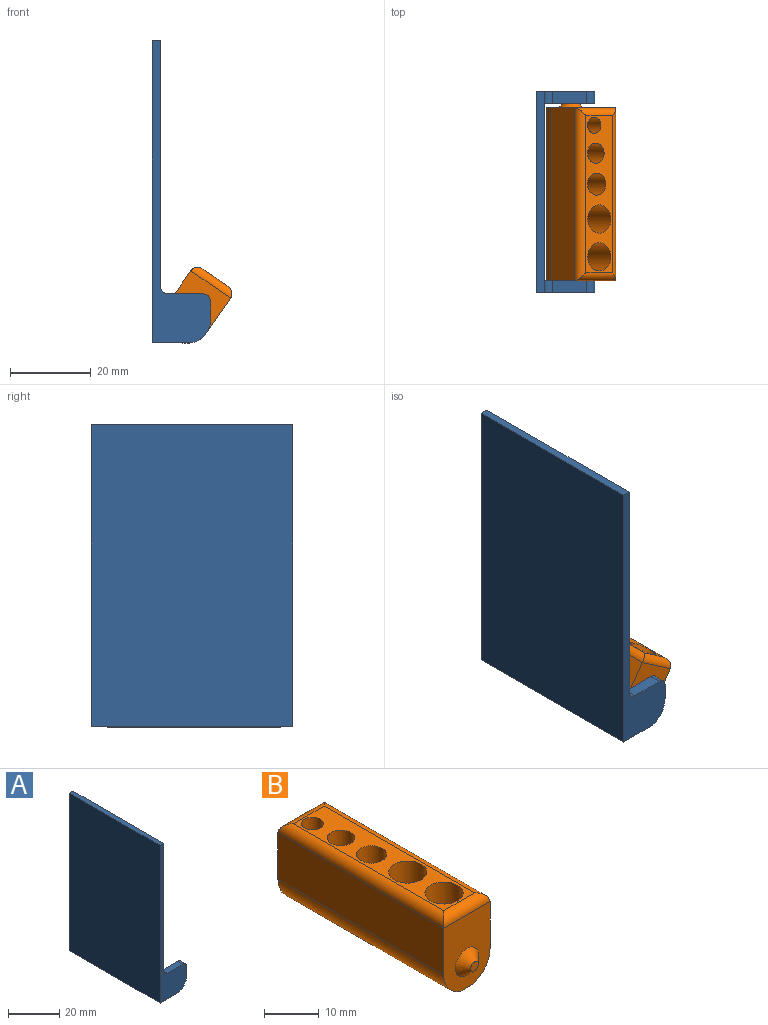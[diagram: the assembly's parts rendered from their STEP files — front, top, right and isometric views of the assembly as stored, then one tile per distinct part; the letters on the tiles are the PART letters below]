
ASSEMBLY  parts=2 mates=1
PART A: 22 faces, bbox 14.6x50x75 mm
  f0: plane 50x2mm, normal (0,0,1), area 100mm2, adj f1,f3,f4,f5
  f1: plane 75x50mm, normal (-1,0,0), area 3750mm2, adj f0,f2,f4,f5
  f2: plane 50x10.14mm, normal (0,0,-1), area 148.8mm2, adj f1,f3,f4,f5,f8,f9,f14,f15
  f3: plane 75x50mm, normal (1,0,0), area 3665.4mm2, adj f0,f2,f4,f5,f9,f15,f18,f21
  f4: plane 75x14.6mm, normal (0,-1,0), area 295.7mm2, adj f0,f1,f2,f3,f6,f7,f8,f20
  f5: plane 75x14.6mm, normal (0,1,0), area 295.7mm2, adj f0,f1,f2,f3,f12,f13,f14,f18
  f6: plane 4.3x3mm, normal (1,0,0), area 12.9mm2, adj f4,f8,f9,f20
  f7: plane 8.6x3mm, normal (0,0,1), area 25.8mm2, adj f4,f9,f20,f21
  f8: cylinder r=6mm len=5.8mm, axis (0,-1,0), area 23.6mm2, adj f2,f4,f6,f9
  f9: plane 14.1x12.6mm, normal (0,1,0), area 117.5mm2, adj f2,f3,f6,f7,f8,f10,f20,f21
  f10: cone r=3mm half-angle=45deg, axis (0,1,0), area 35.5mm2, adj f9,f11
  f11: plane 2x2mm, normal (0,1,0), area 3.1mm2, adj f10
  f12: plane 4.3x3mm, normal (1,0,0), area 12.9mm2, adj f5,f14,f15,f19
  f13: plane 8.6x3mm, normal (0,0,1), area 25.8mm2, adj f5,f15,f18,f19
  f14: cylinder r=6mm len=5.8mm, axis (0,1,0), area 23.6mm2, adj f2,f5,f12,f15
  f15: plane 14.1x12.6mm, normal (0,-1,0), area 117.5mm2, adj f2,f3,f12,f13,f14,f16,f18,f19
  f16: cone r=3mm half-angle=45deg, axis (0,-1,0), area 35.5mm2, adj f15,f17
  f17: plane 2x2mm, normal (0,-1,0), area 3.1mm2, adj f16
  f18: cylinder r=2mm len=3mm, axis (0,-1,0), area 9.4mm2, adj f3,f5,f13,f15
  f19: cylinder r=2mm len=3mm, axis (0,-1,0), area 9.4mm2, adj f5,f12,f13,f15
  f20: cylinder r=2mm len=3mm, axis (0,1,0), area 9.4mm2, adj f4,f6,f7,f9
  f21: cylinder r=2mm len=3mm, axis (0,1,0), area 9.4mm2, adj f3,f4,f7,f9
PART B: 26 faces, bbox 12x47x18.3 mm
  f0: plane 43x10.5mm, normal (-1,0,0), area 451.5mm2, adj f1,f6,f9,f23
  f1: cylinder r=6mm len=43mm, axis (0,1,0), area 338.5mm2, adj f0,f2,f6,f9
  f2: plane 43x3.07mm, normal (0,0,-1), area 132.1mm2, adj f1,f3,f6,f9
  f3: cylinder r=6mm len=43mm, axis (0,1,0), area 338.5mm2, adj f2,f4,f6,f9
  f4: plane 43x10.5mm, normal (1,0,0), area 451.5mm2, adj f3,f6,f9,f24
  f5: plane 39x8mm, normal (0,0,1), area 179.1mm2, adj f12,f14,f16,f18,f20,f22,f23,f24
  f6: plane 16.3x12mm, normal (0,-1,0), area 153.9mm2, adj f0,f1,f2,f3,f4,f7,f22
  f7: cone r=1mm half-angle=45deg, axis (0,1,0), area 35.5mm2, adj f6,f8
  f8: plane 2x2mm, normal (0,-1,0), area 3.1mm2, adj f7
  f9: plane 16.3x12mm, normal (0,1,0), area 153.9mm2, adj f0,f1,f2,f3,f4,f10,f25
  f10: cone r=1mm half-angle=45deg, axis (0,-1,0), area 35.5mm2, adj f9,f11
  f11: plane 2x2mm, normal (0,1,0), area 3.1mm2, adj f10
  f12: cylinder r=3.5mm len=15mm, axis (0,0,1), area 329.9mm2, adj f5,f13
  f13: plane 7x7mm, normal (0,0,1), area 38.5mm2, adj f12
  f14: cylinder r=2mm len=15mm, axis (0,0,1), area 188.5mm2, adj f5,f15
  f15: plane 4x4mm, normal (0,0,1), area 12.6mm2, adj f14
  f16: cylinder r=2.75mm len=15mm, axis (0,0,1), area 259.2mm2, adj f5,f17
  f17: plane 5.5x5.5mm, normal (0,0,1), area 23.8mm2, adj f16
  f18: cylinder r=3.5mm len=15mm, axis (0,0,1), area 329.9mm2, adj f5,f19
  f19: plane 7x7mm, normal (0,0,1), area 38.5mm2, adj f18
  f20: cylinder r=2.5mm len=15mm, axis (0,0,1), area 235.6mm2, adj f5,f21
  f21: plane 5x5mm, normal (0,0,1), area 19.6mm2, adj f20
  f22: cylinder r=2mm len=12mm, axis (1,0,0), area 33.1mm2, adj f5,f6,f23,f24
  f23: cylinder r=2mm len=43mm, axis (0,1,0), area 130.5mm2, adj f0,f5,f22,f25
  f24: cylinder r=2mm len=43mm, axis (0,1,0), area 130.5mm2, adj f4,f5,f22,f25
  f25: cylinder r=2mm len=12mm, axis (1,0,0), area 33.1mm2, adj f5,f9,f23,f24
PLACE A t=(0,0.5,0)mm fixed
PLACE B rot(axis=(0,1,0),34.5deg) t=(0,0,0)mm
MATE revolute A.f10 <-> B.f7  axis (0,1,0) through (0,-21.5,0)mm
